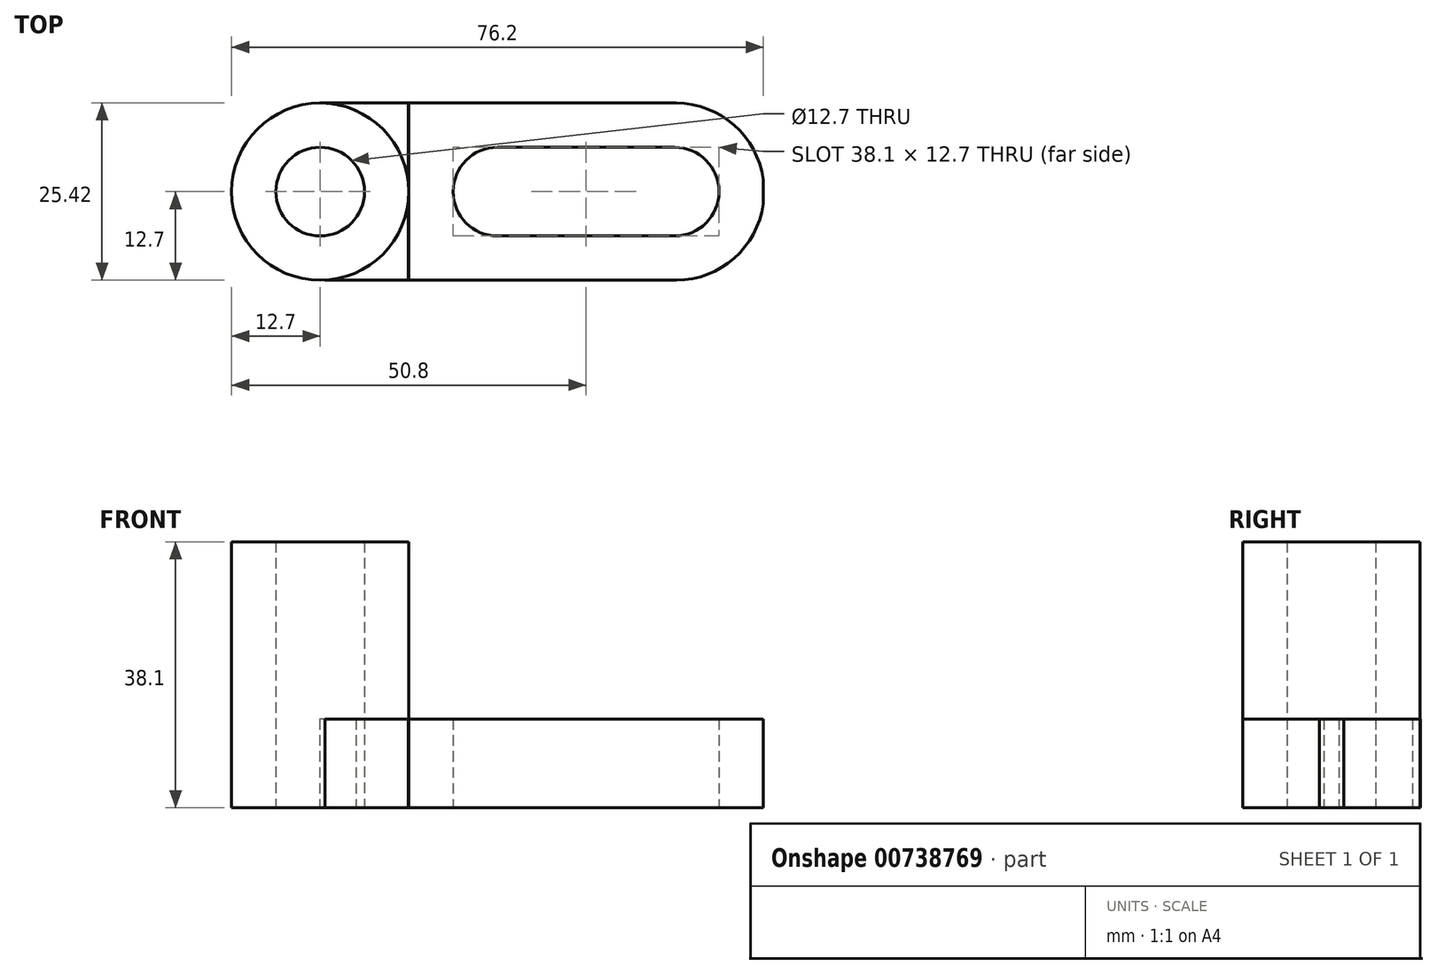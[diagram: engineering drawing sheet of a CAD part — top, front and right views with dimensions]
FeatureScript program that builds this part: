
annotation { "Feature Type Name" : "Feature", "Feature Type Description" : "" }
export const myFeature = defineFeature(function(context is Context, id is Id, definition is map)
    precondition{}
    {
        {
            var Q0;
            Q0=qCreatedBy(makeId("Front.planeOp"),FACE);
            var sketch = newSketch(context, id + "F0", { "sketchPlane" : qUnion([Q0])});
            skLineSegment(sketch, "E0", {"start": v(0, 0) * mm, "end": v(0, 38.1) * mm});
            skLineSegment(sketch, "E1", {"start": v(0, 38.1) * mm, "end": v(25.4, 38.1) * mm});
            skLineSegment(sketch, "E2", {"start": v(25.4, 38.1) * mm, "end": v(25.4, 12.7) * mm});
            skLineSegment(sketch, "E3", {"start": v(25.4, 12.7) * mm, "end": v(76.2, 12.7) * mm});
            skLineSegment(sketch, "E4", {"start": v(76.2, 12.7) * mm, "end": v(76.2, 0) * mm});
            skLineSegment(sketch, "E5", {"start": v(76.2, 0) * mm, "end": v(0, 0) * mm});
            skSolve(sketch);
        }
        {
            var Q0;
            Q0 = qSketchRegion(id + "F0", true);
            extrude(context, id + "F1", {"entities" : qUnion([Q0]), "depth" : 25.4 * mm, "offsetDistance" : 25.4 * mm});
        }
        {
            var Q0;
            Q0=qCreatedBy(makeId("Top.planeOp"),FACE);
            var sketch = newSketch(context, id + "F2", { "sketchPlane" : qUnion([Q0])});
            skLineSegment(sketch, "E6", {"start": v(12.7, 0) * mm, "end": v(12.7, -25.4) * mm});
            skCircle(sketch, "E7", {"center": v(12.7, -12.7) * mm, "radius": 6.35 * mm});
            skSolve(sketch);
        }
        {
            var Q0;
            Q0 = qSketchRegion(id + "F2", true);
            extrude(context, id + "F3", {"entities" : qUnion([Q0]), "operationType" : NewBodyOperationType.REMOVE, "endBound" : BoundingType.THROUGH_ALL, "depth" : 25.4 * mm, "offsetDistance" : 25.4 * mm});
        }
        {
            var Q0;
            Q0=qCreatedBy(makeId("Top.planeOp"),FACE);
            var sketch = newSketch(context, id + "F4", { "sketchPlane" : qUnion([Q0])});
            skLineSegment(sketch, "E8", {"start": v(12.7, 0) * mm, "end": v(12.7, -25.4) * mm});
            skCircle(sketch, "E9", {"center": v(12.7, -12.7) * mm, "radius": 12.7 * mm});
            skLineSegment(sketch, "E10", {"start": v(0, 0) * mm, "end": v(0, -25.4) * mm});
            skLineSegment(sketch, "E11", {"start": v(0, -25.4) * mm, "end": v(12.7, -25.4) * mm});
            skLineSegment(sketch, "E12", {"start": v(0, 0) * mm, "end": v(12.7, 0) * mm});
            skLineSegment(sketch, "E13", {"start": v(12.7, 0) * mm, "end": v(25.4, 0) * mm});
            skLineSegment(sketch, "E14", {"start": v(25.4, 0) * mm, "end": v(25.4, -25.4) * mm});
            skLineSegment(sketch, "E15", {"start": v(25.4, -25.4) * mm, "end": v(12.7, -25.4) * mm});
            skSolve(sketch);
        }
        {
            var Q0;
            {var subQ0=sQuery(id+"F4.wireOp",EDGE,"E12");Q0=makeQuery(id+"F4.imprint","IMPRINT",FACE,{"disambiguationData":[TD([[makeQuery(id+"F4.imprint","IMPRINT",EDGE,{"derivedFrom":subQ0}),-1.0]])]});}
            var Q1;
            {var subQ0=sQuery(id+"F4.wireOp",EDGE,"E11");Q1=makeQuery(id+"F4.imprint","IMPRINT",FACE,{"disambiguationData":[TD([[makeQuery(id+"F4.imprint","IMPRINT",EDGE,{"derivedFrom":subQ0}),1.0]])]});}
            var Q2;
            {var subQ0=sQuery(id+"F4.wireOp",EDGE,"E15");Q2=makeQuery(id+"F4.imprint","IMPRINT",FACE,{"disambiguationData":[TD([[makeQuery(id+"F4.imprint","IMPRINT",EDGE,{"derivedFrom":subQ0}),-1.0]])]});}
            var Q3;
            {var subQ0=sQuery(id+"F4.wireOp",EDGE,"E13");Q3=makeQuery(id+"F4.imprint","IMPRINT",FACE,{"disambiguationData":[TD([[makeQuery(id+"F4.imprint","IMPRINT",EDGE,{"derivedFrom":subQ0}),-1.0]])]});}
            extrude(context, id + "F5", {"entities" : qUnion([Q0, Q1, Q2, Q3]), "operationType" : NewBodyOperationType.REMOVE, "endBound" : BoundingType.THROUGH_ALL, "depth" : 25.4 * mm, "offsetDistance" : 25.4 * mm});
        }
        {
            var Q0;
            Q0=qCreatedBy(makeId("Top.planeOp"),FACE);
            var sketch = newSketch(context, id + "F6", { "sketchPlane" : qUnion([Q0])});
            skLineSegment(sketch, "E16", {"start": v(25.35, 0.02) * mm, "end": v(12.65, 0.02) * mm});
            skLineSegment(sketch, "E17", {"start": v(25.35, 0.02) * mm, "end": v(25.35, -25.38) * mm});
            skLineSegment(sketch, "E18", {"start": v(25.35, -25.38) * mm, "end": v(12.65, -25.38) * mm});
            skArc(sketch, "E19", {"start": v(12.65, -25.38) * mm, "mid": v(25.35, -12.68) * mm, "end": v(12.65, 0.02) * mm});
            skSolve(sketch);
        }
        {
            var Q0;
            Q0 = qSketchRegion(id + "F6", true);
            extrude(context, id + "F7", {"entities" : qUnion([Q0]), "operationType" : NewBodyOperationType.ADD, "depth" : 12.7 * mm, "offsetDistance" : 25.4 * mm});
        }
        {
            var Q0;
            Q0=qCreatedBy(makeId("Top.planeOp"),FACE);
            var sketch = newSketch(context, id + "F8", { "sketchPlane" : qUnion([Q0])});
            skLineSegment(sketch, "E20", {"start": v(38.1, 0) * mm, "end": v(38.1, -25.4) * mm});
            skLineSegment(sketch, "E21", {"start": v(63.5, 0) * mm, "end": v(63.5, -25.4) * mm});
            skCircle(sketch, "E22", {"center": v(38.1, -12.7) * mm, "radius": 6.35 * mm});
            skCircle(sketch, "E23", {"center": v(63.5, -12.7) * mm, "radius": 6.35 * mm});
            skLineSegment(sketch, "E24", {"start": v(38.1, -6.35) * mm, "end": v(63.5, -6.35) * mm});
            skLineSegment(sketch, "E25", {"start": v(38.1, -19.05) * mm, "end": v(63.5, -19.05) * mm});
            skArc(sketch, "E26", {"start": v(63.5, -25.4) * mm, "mid": v(76.32, -12.7) * mm, "end": v(63.5, 0) * mm});
            skLineSegment(sketch, "E27", {"start": v(63.5, 0) * mm, "end": v(77.4, 0.13) * mm});
            skLineSegment(sketch, "E28", {"start": v(77.4, 0.13) * mm, "end": v(77.63, -25.42) * mm});
            skLineSegment(sketch, "E29", {"start": v(77.63, -25.42) * mm, "end": v(63.5, -25.4) * mm});
            skSolve(sketch);
        }
        {
            var Q0;
            {var subQ0=sQuery(id+"F8.wireOp",EDGE,"E22");var subQ1=sQuery(id+"F8.wireOp",EDGE,"E20");var subQ2=makeQuery(id+"F8.imprint","INTERSECT",VERTEX,{"derivedFrom":[subQ1,subQ0,sQuery(id+"F8.wireOp",EDGE,"E24")]});Q0=makeQuery(id+"F8.imprint","IMPRINT",FACE,{"disambiguationData":[TD([[makeQuery(id+"F8.imprint","IMPRINT",EDGE,{"disambiguationData":[TD([[subQ2,-1.0]])],"derivedFrom":subQ1}),-1.0]])]});}
            var Q1;
            {var subQ0=sQuery(id+"F8.wireOp",EDGE,"E29");var subQ1=sQuery(id+"F8.wireOp",EDGE,"E26");var subQ3=makeQuery(id+"F8.imprint","INTERSECT",VERTEX,{"derivedFrom":[subQ1,subQ0]});Q1=makeQuery(id+"F8.imprint","IMPRINT",FACE,{"disambiguationData":[TD([[makeQuery(id+"F8.imprint","IMPRINT",EDGE,{"disambiguationData":[TD([[subQ3,1.0]])],"derivedFrom":subQ1}),1.0]])]});}
            var Q2;
            {var subQ0=sQuery(id+"F8.wireOp",EDGE,"E27");Q2=makeQuery(id+"F8.imprint","IMPRINT",FACE,{"disambiguationData":[TD([[makeQuery(id+"F8.imprint","IMPRINT",EDGE,{"derivedFrom":subQ0}),-1.0]])]});}
            var Q3;
            {var subQ0=sQuery(id+"F8.wireOp",EDGE,"E22");var subQ1=sQuery(id+"F8.wireOp",EDGE,"E20");var subQ2=makeQuery(id+"F8.imprint","INTERSECT",VERTEX,{"derivedFrom":[subQ1,subQ0,sQuery(id+"F8.wireOp",EDGE,"E24")]});Q3=makeQuery(id+"F8.imprint","IMPRINT",FACE,{"disambiguationData":[TD([[makeQuery(id+"F8.imprint","IMPRINT",EDGE,{"disambiguationData":[TD([[subQ2,-1.0]])],"derivedFrom":subQ1}),1.0]])]});}
            var Q4;
            {var subQ0=sQuery(id+"F8.wireOp",EDGE,"E23");var subQ1=sQuery(id+"F8.wireOp",EDGE,"E21");var subQ2=makeQuery(id+"F8.imprint","INTERSECT",VERTEX,{"derivedFrom":[subQ1,subQ0,sQuery(id+"F8.wireOp",EDGE,"E24")]});Q4=makeQuery(id+"F8.imprint","IMPRINT",FACE,{"disambiguationData":[TD([[makeQuery(id+"F8.imprint","IMPRINT",EDGE,{"disambiguationData":[TD([[subQ2,-1.0]])],"derivedFrom":subQ1}),-1.0]])]});}
            var Q5;
            {var subQ0=sQuery(id+"F8.wireOp",EDGE,"E23");var subQ1=sQuery(id+"F8.wireOp",EDGE,"E21");var subQ2=makeQuery(id+"F8.imprint","INTERSECT",VERTEX,{"derivedFrom":[subQ1,subQ0,sQuery(id+"F8.wireOp",EDGE,"E24")]});Q5=makeQuery(id+"F8.imprint","IMPRINT",FACE,{"disambiguationData":[TD([[makeQuery(id+"F8.imprint","IMPRINT",EDGE,{"disambiguationData":[TD([[subQ2,-1.0]])],"derivedFrom":subQ1}),1.0]])]});}
            var Q6;
            {var subQ0=sQuery(id+"F8.wireOp",EDGE,"E24");Q6=makeQuery(id+"F8.imprint","IMPRINT",FACE,{"disambiguationData":[TD([[makeQuery(id+"F8.imprint","IMPRINT",EDGE,{"derivedFrom":subQ0}),-1.0]])]});}
            extrude(context, id + "F9", {"entities" : qUnion([Q0, Q1, Q2, Q3, Q4, Q5, Q6]), "operationType" : NewBodyOperationType.REMOVE, "endBound" : BoundingType.THROUGH_ALL, "depth" : 25.4 * mm, "offsetDistance" : 25.4 * mm});
        }
    });
